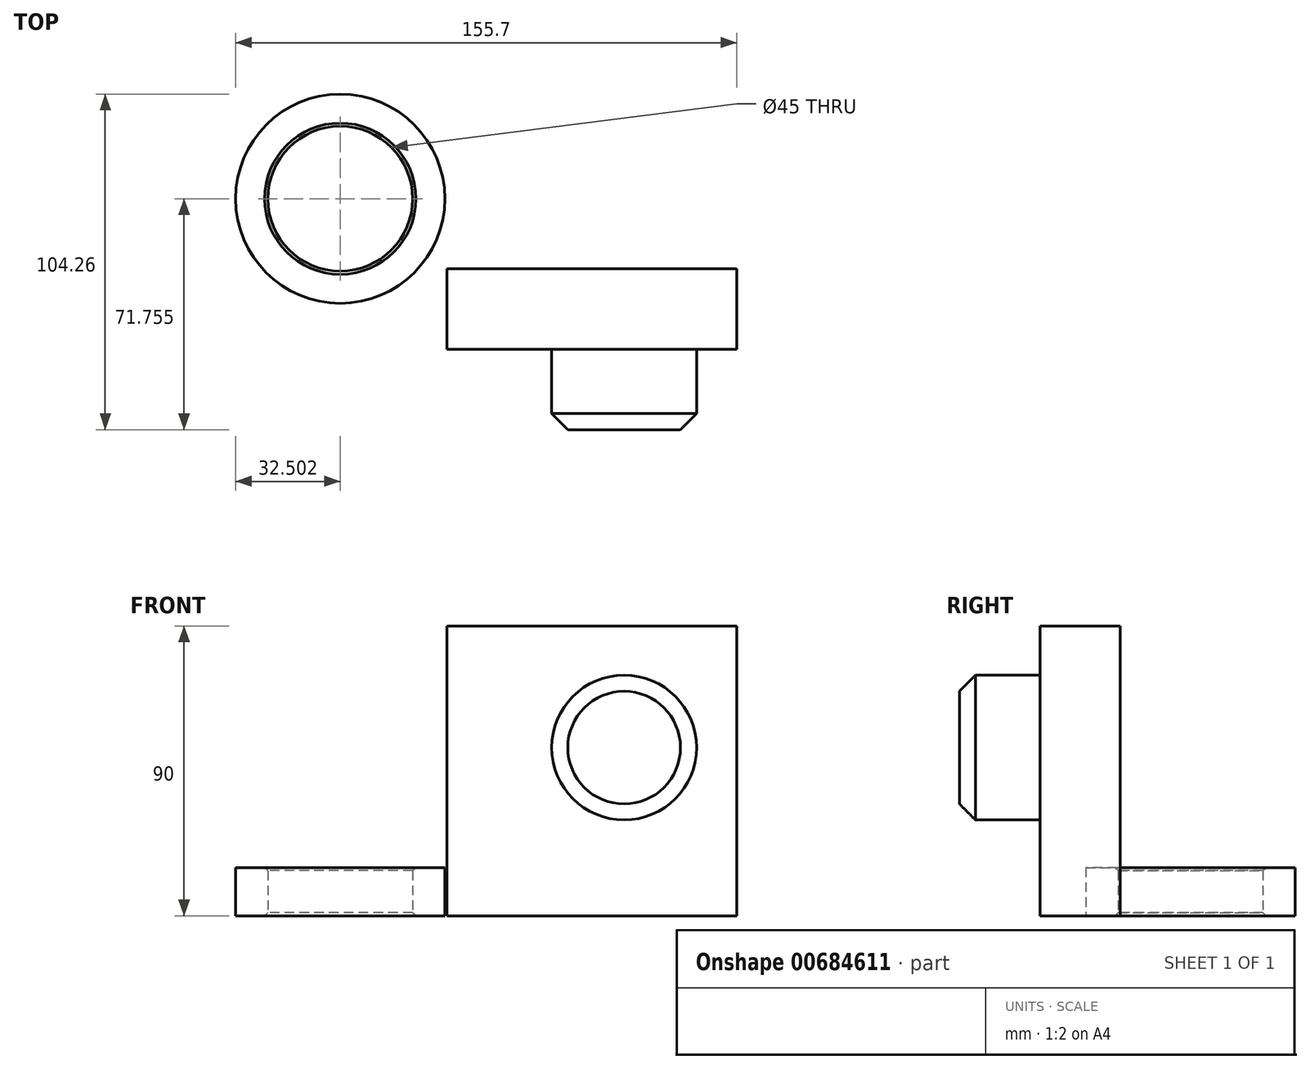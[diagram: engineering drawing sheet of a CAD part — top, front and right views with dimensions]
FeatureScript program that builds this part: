
annotation { "Feature Type Name" : "Feature", "Feature Type Description" : "" }
export const myFeature = defineFeature(function(context is Context, id is Id, definition is map)
    precondition{}
    {
        {
            var Q0;
            Q0=qCreatedBy(makeId("Front.planeOp"),FACE);
            var sketch = newSketch(context, id + "F0", { "sketchPlane" : qUnion([Q0])});
            skLineSegment(sketch, "E0.bottom", {"start": v(0, 0) * mm, "end": v(90, 0) * mm});
            skLineSegment(sketch, "E0.top", {"start": v(0, 90) * mm, "end": v(90, 90) * mm});
            skLineSegment(sketch, "E0.left", {"start": v(0, 0) * mm, "end": v(0, 90) * mm});
            skLineSegment(sketch, "E0.right", {"start": v(90, 0) * mm, "end": v(90, 90) * mm});
            skSolve(sketch);
        }
        {
            var Q0;
            Q0=makeQuery(id+"F0.imprint","IMPRINT",FACE,{"disambiguationData":[TD([[makeQuery(id+"F0.imprint","IMPRINT",EDGE,{"derivedFrom":sQuery(id+"F0.wireOp",EDGE,"E0.bottom")}),1.0]])]});
            extrude(context, id + "F1", {"entities" : qUnion([Q0]), "depth" : 25 * mm, "offsetDistance" : 25 * mm});
        }
        {
            var Q0;
            Q0=makeQuery(id+"F1.opExtrude","CAP_FACE",FACE,{"disambiguationData":[OSD([sQuery(id+"F0.wireOp",EDGE,"E0.bottom"),sQuery(id+"F0.wireOp",EDGE,"E0.top"),sQuery(id+"F0.wireOp",EDGE,"E0.left"),sQuery(id+"F0.wireOp",EDGE,"E0.right")])],"isStart":false});
            var sketch = newSketch(context, id + "F2", { "sketchPlane" : qUnion([Q0])});
            skCircle(sketch, "E1", {"center": v(55, 52.24) * mm, "radius": 22.5 * mm});
            skSolve(sketch);
        }
        {
            var Q0;
            Q0 = qSketchRegion(id + "F2", true);
            var sketch = newSketch(context, id + "F3", { "sketchPlane" : qUnion([Q0])});
            skSolve(sketch);
        }
        {
            var Q0;
            Q0=makeQuery(id+"F3.imprint","IMPRINT",FACE,{"disambiguationData":[TD([[makeQuery(id+"F3.imprint","IMPRINT",EDGE,{"derivedFrom":makeQuery(id+"F2.imprint","IMPRINT",EDGE,{"derivedFrom":sQuery(id+"F2.wireOp",EDGE,"E1")})}),1.0]])]});
            extrude(context, id + "F4", {"entities" : qUnion([Q0]), "operationType" : NewBodyOperationType.ADD, "depth" : 25 * mm, "offsetDistance" : 25 * mm});
        }
        {
            var Q0;
            Q0=qCreatedBy(makeId("Top.planeOp"),FACE);
            var sketch = newSketch(context, id + "F5", { "sketchPlane" : qUnion([Q0])});
            skCircle(sketch, "E2", {"center": v(-33.2, 21.76) * mm, "radius": 32.5 * mm});
            skCircle(sketch, "E3", {"center": v(-33.2, 21.76) * mm, "radius": 22.5 * mm});
            skSolve(sketch);
        }
        {
            var Q0;
            Q0 = qSketchRegion(id + "F5", true);
            extrude(context, id + "F6", {"entities" : qUnion([Q0]), "depth" : 15 * mm, "offsetDistance" : 25 * mm});
        }
        {
            var Q0;
            Q0=makeQuery(id+"F4.opExtrude","CAP_EDGE",EDGE,{"disambiguationData":[OSD([sQuery(id+"F2.wireOp",EDGE,"E1")])],"isStart":false});
            chamfer(context, id + "F7", {"entities" : qUnion([Q0]), "width" : 5 * mm, "tangentPropagation" : true});
        }
        {
            var Q0;
            Q0=makeQuery(id+"F6.opExtrude","CAP_EDGE",EDGE,{"disambiguationData":[OSD([sQuery(id+"F5.wireOp",EDGE,"E3")])],"isStart":false});
            var Q1;
            Q1=makeQuery(id+"F6.opExtrude","CAP_EDGE",EDGE,{"disambiguationData":[OSD([sQuery(id+"F5.wireOp",EDGE,"E3")])],"isStart":true});
            chamfer(context, id + "F8", {"entities" : qUnion([Q0, Q1]), "width" : 1 * mm, "tangentPropagation" : true});
        }
    });
